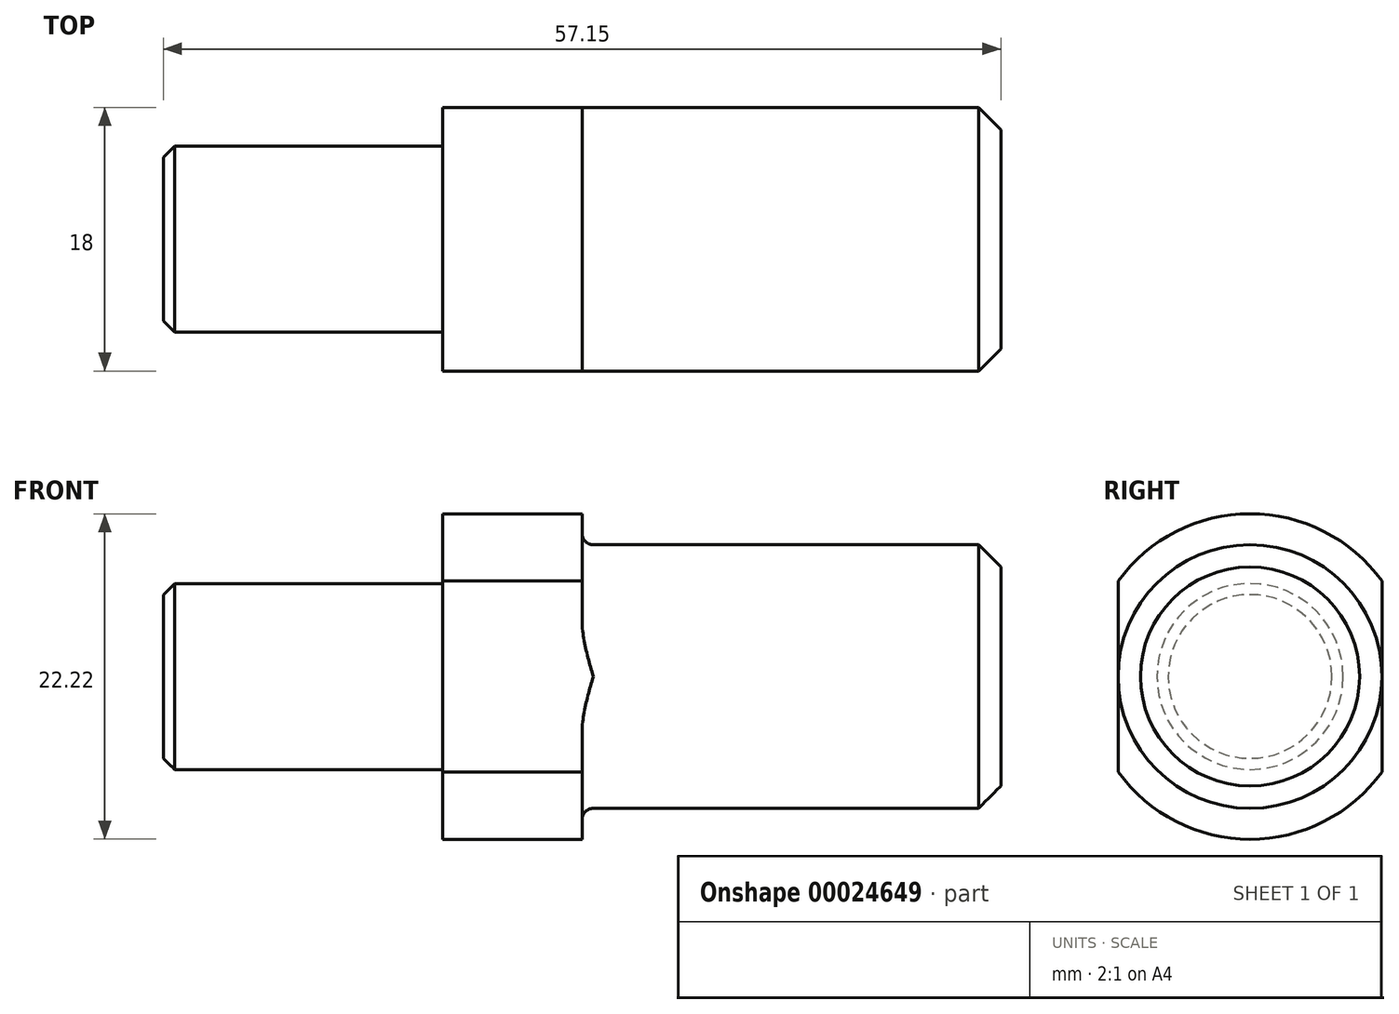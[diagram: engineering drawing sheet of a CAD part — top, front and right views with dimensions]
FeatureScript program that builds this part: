
annotation { "Feature Type Name" : "Feature", "Feature Type Description" : "" }
export const myFeature = defineFeature(function(context is Context, id is Id, definition is map)
    precondition{}
    {
        {
            var Q0;
            Q0=qCreatedBy(makeId("Right.planeOp"),FACE);
            var sketch = newSketch(context, id + "F0", { "sketchPlane" : qUnion([Q0])});
            skCircle(sketch, "E0", {"center": v(0, 0) * mm, "radius": 6.35 * mm});
            skSolve(sketch);
        }
        {
            var Q0;
            Q0 = qSketchRegion(id + "F0", true);
            extrude(context, id + "F1", {"entities" : qUnion([Q0]), "oppositeDirection" : true, "depth" : 19.05 * mm});
        }
        {
            var Q0;
            Q0=makeQuery(id+"F1.opExtrude","CAP_EDGE",EDGE,{"disambiguationData":[OSD([sQuery(id+"F0.wireOp",EDGE,"E0")])],"isStart":false});
            chamfer(context, id + "F2", {"entities" : qUnion([Q0]), "width" : 0.76 * mm, "tangentPropagation" : true});
        }
        {
            var Q0;
            Q0=qCreatedBy(makeId("Right.planeOp"),FACE);
            var sketch = newSketch(context, id + "F3", { "sketchPlane" : qUnion([Q0])});
            skCircle(sketch, "E1", {"center": v(0, 0) * mm, "radius": 9 * mm});
            skSolve(sketch);
        }
        {
            var Q0;
            Q0=makeQuery(id+"F3.imprint","IMPRINT",FACE,{"disambiguationData":[TD([[makeQuery(id+"F3.imprint","IMPRINT",EDGE,{"derivedFrom":sQuery(id+"F3.wireOp",EDGE,"E1")}),1.0]])]});
            extrude(context, id + "F4", {"entities" : qUnion([Q0]), "operationType" : NewBodyOperationType.ADD, "depth" : 38.1 * mm});
        }
        {
            var Q0;
            Q0=qCreatedBy(makeId("Right.planeOp"),FACE);
            var sketch = newSketch(context, id + "F5", { "sketchPlane" : qUnion([Q0])});
            skCircle(sketch, "E2", {"center": v(0, 0) * mm, "radius": 11.11 * mm});
            skSolve(sketch);
        }
        {
            var Q0;
            Q0 = qSketchRegion(id + "F5", true);
            extrude(context, id + "F6", {"entities" : qUnion([Q0]), "operationType" : NewBodyOperationType.ADD, "depth" : 9.52 * mm});
        }
        {
            var Q0;
            Q0=makeQuery(id+"F6.boolean.opBoolean","INTERSECT",EDGE,{"derivedFrom":[makeQuery(id+"F4.opExtrude","SWEPT_FACE",FACE,{"disambiguationData":[OSD([sQuery(id+"F3.wireOp",EDGE,"E1")])]}),makeQuery(id+"F6.opExtrude","CAP_FACE",FACE,{"disambiguationData":[OSD([sQuery(id+"F5.wireOp",EDGE,"E2")])],"isStart":false})]});
            fillet(context, id + "F7", {"entities" : qUnion([Q0]), "radius" : 0.76 * mm, "tangentPropagation" : true, "allowEdgeOverflow" : false});
        }
        {
            var Q0;
            Q0=makeQuery(id+"F4.opExtrude","CAP_FACE",FACE,{"disambiguationData":[OSD([sQuery(id+"F3.wireOp",EDGE,"E1")])],"isStart":false});
            chamfer(context, id + "F8", {"entities" : qUnion([Q0]), "width" : 1.52 * mm, "tangentPropagation" : true});
        }
        {
            var Q0;
            Q0=qCreatedBy(makeId("Top.planeOp"),FACE);
            var sketch = newSketch(context, id + "F9", { "sketchPlane" : qUnion([Q0])});
            skLineSegment(sketch, "E3", {"start": v(10.29, 9) * mm, "end": v(36.58, 9) * mm, "construction": true});
            skLineSegment(sketch, "E4.bottom", {"start": v(10.29, 9) * mm, "end": v(-2.96, 9) * mm});
            skLineSegment(sketch, "E4.top", {"start": v(10.29, 13.67) * mm, "end": v(-2.96, 13.67) * mm});
            skLineSegment(sketch, "E4.left", {"start": v(10.29, 9) * mm, "end": v(10.29, 13.67) * mm});
            skLineSegment(sketch, "E4.right", {"start": v(-2.96, 9) * mm, "end": v(-2.96, 13.67) * mm});
            skLineSegment(sketch, "E5", {"start": v(-21.58, 0) * mm, "end": v(40.55, 0) * mm, "construction": true});
            skLineSegment(sketch, "E6.MirrorCS", {"start": v(10.29, -9) * mm, "end": v(-2.96, -9) * mm});
            skLineSegment(sketch, "E7.MirrorCS", {"start": v(10.29, -13.67) * mm, "end": v(-2.96, -13.67) * mm});
            skLineSegment(sketch, "E8.MirrorCS", {"start": v(10.29, -9) * mm, "end": v(10.29, -13.67) * mm});
            skLineSegment(sketch, "E9.MirrorCS", {"start": v(-2.96, -9) * mm, "end": v(-2.96, -13.67) * mm});
            skSolve(sketch);
        }
        {
            var Q0;
            Q0 = qSketchRegion(id + "F9", true);
            extrude(context, id + "F10", {"entities" : qUnion([Q0]), "operationType" : NewBodyOperationType.REMOVE, "endBound" : BoundingType.THROUGH_ALL, "oppositeDirection" : true, "depth" : 25.4 * mm, "hasSecondDirection" : true, "secondDirectionBound" : SecondDirectionBoundingType.THROUGH_ALL, "secondDirectionOppositeDirection" : false, "secondDirectionDepth" : 25.4 * mm});
        }
    });
